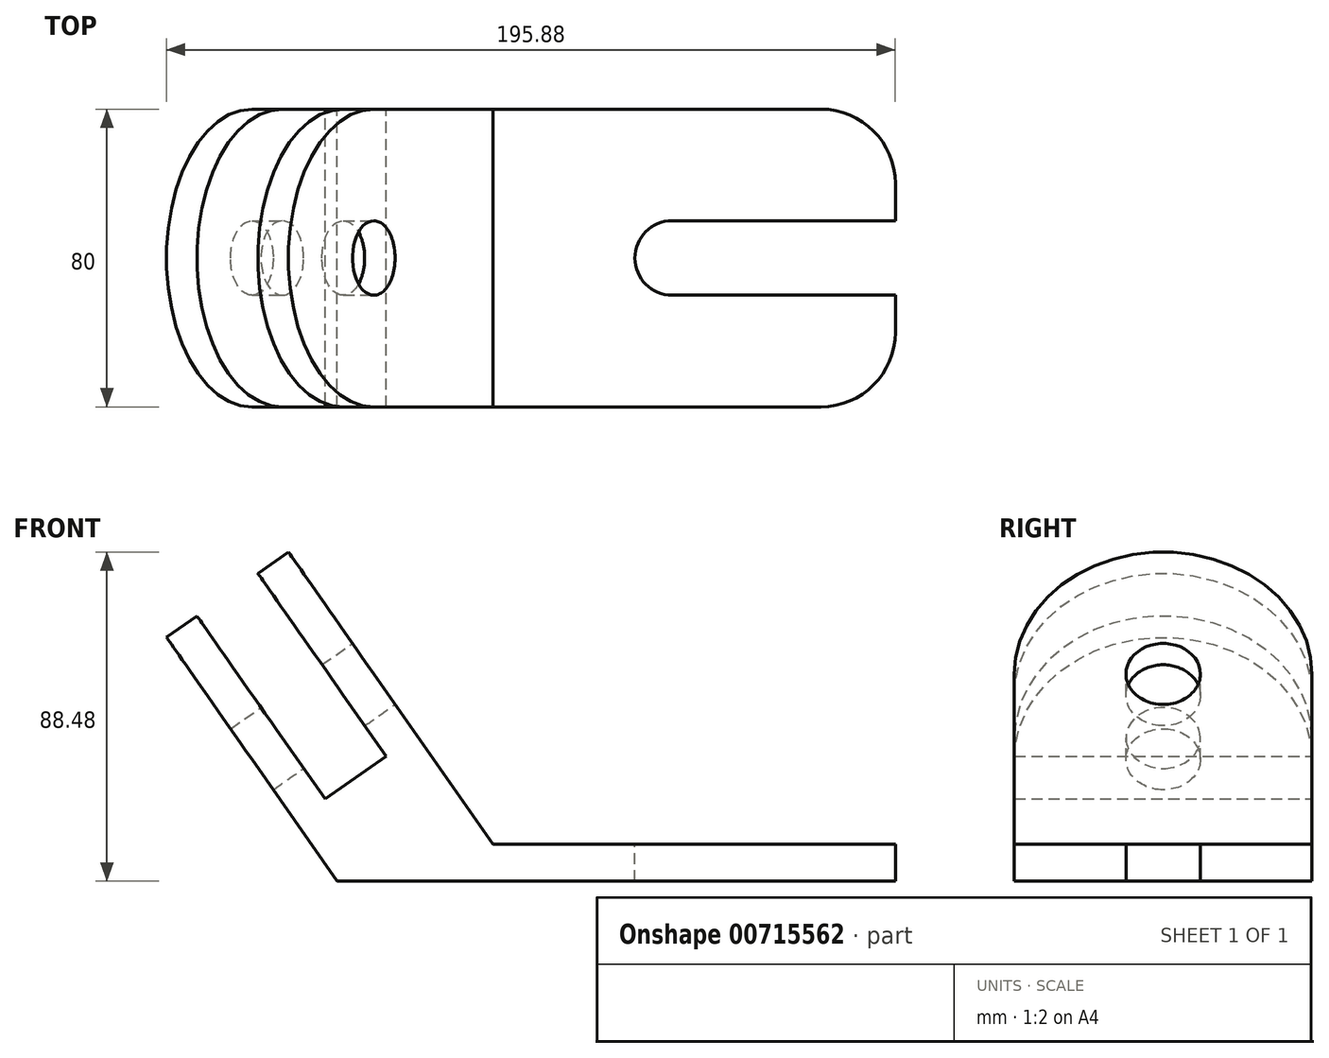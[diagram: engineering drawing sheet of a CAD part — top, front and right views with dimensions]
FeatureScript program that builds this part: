
annotation { "Feature Type Name" : "Feature", "Feature Type Description" : "" }
export const myFeature = defineFeature(function(context is Context, id is Id, definition is map)
    precondition{}
    {
        {
            var Q0;
            Q0=qCreatedBy(makeId("Front.planeOp"),FACE);
            var sketch = newSketch(context, id + "F0", { "sketchPlane" : qUnion([Q0])});
            skLineSegment(sketch, "E0", {"start": v(-75.24, 0) * mm, "end": v(74.76, 0) * mm});
            skLineSegment(sketch, "E1", {"start": v(74.76, 0) * mm, "end": v(74.76, 10) * mm});
            skLineSegment(sketch, "E2", {"start": v(74.76, 10) * mm, "end": v(-25.24, 10) * mm});
            skLineSegment(sketch, "E3", {"start": v(-75.24, 0) * mm, "end": v(-121.12, 65.53) * mm});
            skLineSegment(sketch, "E4", {"start": v(-121.12, 65.53) * mm, "end": v(-112.93, 71.27) * mm});
            skLineSegment(sketch, "E5", {"start": v(-112.93, 71.27) * mm, "end": v(-78.52, 22.12) * mm});
            skLineSegment(sketch, "E6", {"start": v(-78.52, 22.12) * mm, "end": v(-62.13, 33.6) * mm});
            skLineSegment(sketch, "E7", {"start": v(-62.13, 33.6) * mm, "end": v(-96.55, 82.74) * mm});
            skLineSegment(sketch, "E8", {"start": v(-96.55, 82.74) * mm, "end": v(-88.36, 88.48) * mm});
            skLineSegment(sketch, "E9", {"start": v(-88.36, 88.48) * mm, "end": v(-33.4, 10) * mm});
            skLineSegment(sketch, "E10", {"start": v(-33.4, 10) * mm, "end": v(-25.24, 10) * mm});
            skSolve(sketch);
        }
        {
            var Q0;
            Q0=makeQuery(id+"F0.imprint","IMPRINT",FACE,{"disambiguationData":[TD([[makeQuery(id+"F0.imprint","IMPRINT",EDGE,{"derivedFrom":sQuery(id+"F0.wireOp",EDGE,"E0")}),1.0]])]});
            extrude(context, id + "F1", {"entities" : qUnion([Q0]), "depth" : 80 * mm, "offsetDistance" : 25 * mm});
        }
        {
            var Q0;
            Q0=makeQuery(id+"F1.opExtrude","CAP_EDGE",EDGE,{"disambiguationData":[OSD([sQuery(id+"F0.wireOp",EDGE,"E8")])],"isStart":false});
            var Q1;
            Q1=makeQuery(id+"F1.opExtrude","CAP_EDGE",EDGE,{"disambiguationData":[OSD([sQuery(id+"F0.wireOp",EDGE,"E4")])],"isStart":false});
            var Q2;
            Q2=makeQuery(id+"F1.opExtrude","CAP_EDGE",EDGE,{"disambiguationData":[OSD([sQuery(id+"F0.wireOp",EDGE,"E8")])],"isStart":true});
            var Q3;
            Q3=makeQuery(id+"F1.opExtrude","CAP_EDGE",EDGE,{"disambiguationData":[OSD([sQuery(id+"F0.wireOp",EDGE,"E4")])],"isStart":true});
            fillet(context, id + "F2", {"entities" : qUnion([Q0, Q1, Q2, Q3]), "radius" : 40 * mm, "tangentPropagation" : true, "allowEdgeOverflow" : false});
        }
        {
            var Q0;
            Q0=makeQuery(id+"F1.opExtrude","SWEPT_FACE",FACE,{"disambiguationData":[OSD([sQuery(id+"F0.wireOp",EDGE,"E2"),sQuery(id+"F0.wireOp",EDGE,"E10")])]});
            var sketch = newSketch(context, id + "F3", { "sketchPlane" : qUnion([Q0])});
            skLineSegment(sketch, "E11.bottom", {"start": v(14.76, -50) * mm, "end": v(134.76, -50) * mm});
            skLineSegment(sketch, "E11.top", {"start": v(14.76, -30) * mm, "end": v(134.76, -30) * mm});
            skLineSegment(sketch, "E11.left", {"start": v(14.76, -50) * mm, "end": v(14.76, -30) * mm});
            skLineSegment(sketch, "E11.right", {"start": v(134.76, -50) * mm, "end": v(134.76, -30) * mm});
            skPoint(sketch, "E11.middle", {"position": v(74.76, -40) * mm});
            skCircle(sketch, "E12", {"center": v(14.76, -40) * mm, "radius": 10 * mm});
            skSolve(sketch);
        }
        {
            var Q0;
            Q0 = qSketchRegion(id + "F3", true);
            extrude(context, id + "F4", {"entities" : qUnion([Q0]), "operationType" : NewBodyOperationType.REMOVE, "oppositeDirection" : true, "depth" : 25 * mm, "offsetDistance" : 25 * mm});
        }
        {
            var Q0;
            Q0=makeQuery(id+"F1.opExtrude","CAP_EDGE",EDGE,{"disambiguationData":[OSD([sQuery(id+"F0.wireOp",EDGE,"E1")])],"isStart":true});
            var Q1;
            Q1=makeQuery(id+"F1.opExtrude","CAP_EDGE",EDGE,{"disambiguationData":[OSD([sQuery(id+"F0.wireOp",EDGE,"E1")])],"isStart":false});
            fillet(context, id + "F5", {"entities" : qUnion([Q0, Q1]), "radius" : 20 * mm, "tangentPropagation" : true, "allowEdgeOverflow" : false});
        }
        {
            var Q0;
            Q0=makeQuery(id+"F1.opExtrude","SWEPT_FACE",FACE,{"disambiguationData":[OSD([sQuery(id+"F0.wireOp",EDGE,"E9")])]});
            var sketch = newSketch(context, id + "F6", { "sketchPlane" : qUnion([Q0])});
            skCircle(sketch, "E13", {"center": v(-40, 83.15) * mm, "radius": 10 * mm});
            skSolve(sketch);
        }
        {
            var Q0;
            Q0 = qSketchRegion(id + "F6", true);
            extrude(context, id + "F7", {"entities" : qUnion([Q0]), "operationType" : NewBodyOperationType.REMOVE, "oppositeDirection" : true, "depth" : 57.1 * mm, "offsetDistance" : 25 * mm});
        }
    });
